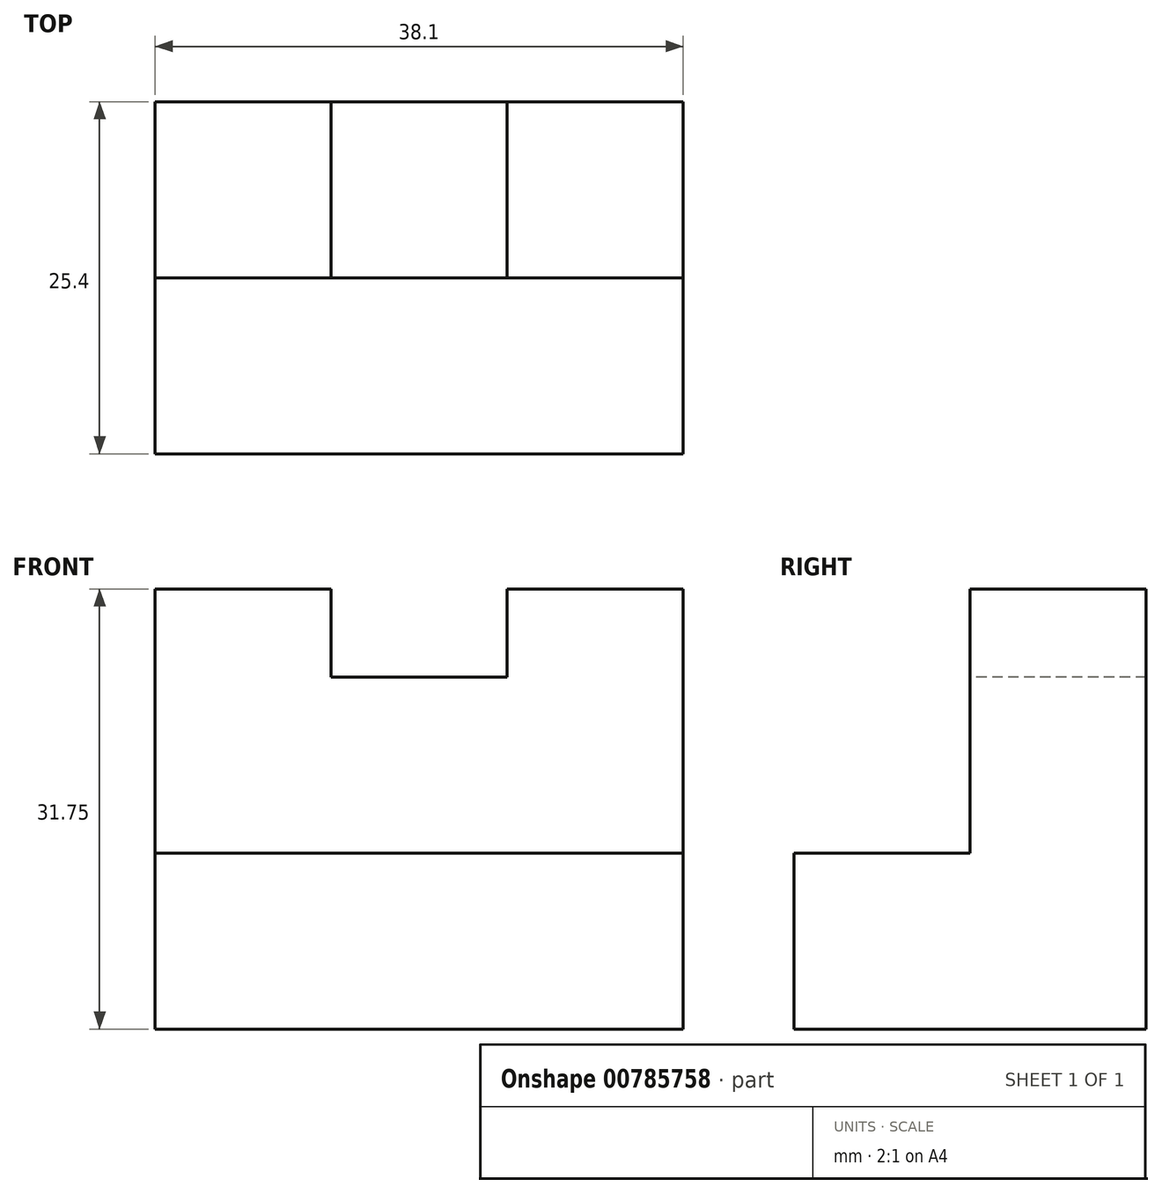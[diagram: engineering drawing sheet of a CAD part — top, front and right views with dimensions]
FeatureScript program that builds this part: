
annotation { "Feature Type Name" : "Feature", "Feature Type Description" : "" }
export const myFeature = defineFeature(function(context is Context, id is Id, definition is map)
    precondition{}
    {
        {
            var Q0;
            Q0=qCreatedBy(makeId("Front.planeOp"),FACE);
            var sketch = newSketch(context, id + "F0", { "sketchPlane" : qUnion([Q0])});
            skLineSegment(sketch, "E0", {"start": v(0, 0) * mm, "end": v(38.1, 0) * mm});
            skLineSegment(sketch, "E1", {"start": v(0, 0) * mm, "end": v(0, 31.75) * mm});
            skLineSegment(sketch, "E2", {"start": v(0, 31.75) * mm, "end": v(38.1, 31.75) * mm});
            skLineSegment(sketch, "E3", {"start": v(38.1, 31.75) * mm, "end": v(38.1, 0) * mm});
            skSolve(sketch);
        }
        {
            var Q0;
            Q0=makeQuery(id+"F0.imprint","IMPRINT",FACE,{"disambiguationData":[TD([[makeQuery(id+"F0.imprint","IMPRINT",EDGE,{"derivedFrom":sQuery(id+"F0.wireOp",EDGE,"E0")}),1.0]])]});
            extrude(context, id + "F1", {"entities" : qUnion([Q0]), "depth" : 25.4 * mm, "offsetDistance" : 25.4 * mm});
        }
        {
            var Q0;
            Q0=makeQuery(id+"F1.opExtrude","SWEPT_FACE",FACE,{"disambiguationData":[OSD([sQuery(id+"F0.wireOp",EDGE,"E3")])]});
            var sketch = newSketch(context, id + "F2", { "sketchPlane" : qUnion([Q0])});
            skLineSegment(sketch, "E4", {"start": v(-25.4, 0) * mm, "end": v(-25.4, 12.7) * mm});
            skLineSegment(sketch, "E5", {"start": v(-25.4, 12.7) * mm, "end": v(-12.7, 12.7) * mm});
            skLineSegment(sketch, "E6", {"start": v(-12.7, 12.7) * mm, "end": v(-12.7, 31.75) * mm});
            skLineSegment(sketch, "E7", {"start": v(-12.7, 31.75) * mm, "end": v(0, 31.75) * mm});
            skSolve(sketch);
        }
        {
            var Q0;
            {var subQ0=sQuery(id+"F2.wireOp",EDGE,"E5");Q0=makeQuery(id+"F2.imprint","IMPRINT",FACE,{"disambiguationData":[TD([[makeQuery(id+"F2.imprint","IMPRINT",EDGE,{"derivedFrom":subQ0}),1.0]])]});}
            extrude(context, id + "F3", {"entities" : qUnion([Q0]), "operationType" : NewBodyOperationType.REMOVE, "oppositeDirection" : true, "depth" : 38.1 * mm, "offsetDistance" : 25.4 * mm});
        }
        {
            var Q0;
            Q0=makeQuery(id+"F3.boolean.opBoolean","COPY",FACE,{"derivedFrom":makeQuery(id+"F3.opExtrude","SWEPT_FACE",FACE,{"disambiguationData":[OSD([sQuery(id+"F2.wireOp",EDGE,"E6")])]})});
            var sketch = newSketch(context, id + "F4", { "sketchPlane" : qUnion([Q0])});
            skLineSegment(sketch, "E8", {"start": v(0, 31.75) * mm, "end": v(12.7, 31.75) * mm});
            skLineSegment(sketch, "E9", {"start": v(38.1, 31.75) * mm, "end": v(25.4, 31.75) * mm});
            skLineSegment(sketch, "E10", {"start": v(12.7, 31.75) * mm, "end": v(12.7, 25.4) * mm});
            skLineSegment(sketch, "E11", {"start": v(12.7, 25.4) * mm, "end": v(25.4, 25.4) * mm});
            skLineSegment(sketch, "E12", {"start": v(25.4, 31.75) * mm, "end": v(25.4, 25.4) * mm});
            skSolve(sketch);
        }
        {
            var Q0;
            {var subQ0=sQuery(id+"F4.wireOp",EDGE,"E10");Q0=makeQuery(id+"F4.imprint","IMPRINT",FACE,{"disambiguationData":[TD([[makeQuery(id+"F4.imprint","IMPRINT",EDGE,{"derivedFrom":subQ0}),1.0]])]});}
            extrude(context, id + "F5", {"entities" : qUnion([Q0]), "operationType" : NewBodyOperationType.REMOVE, "oppositeDirection" : true, "depth" : 25.4 * mm, "offsetDistance" : 25.4 * mm});
        }
    });
